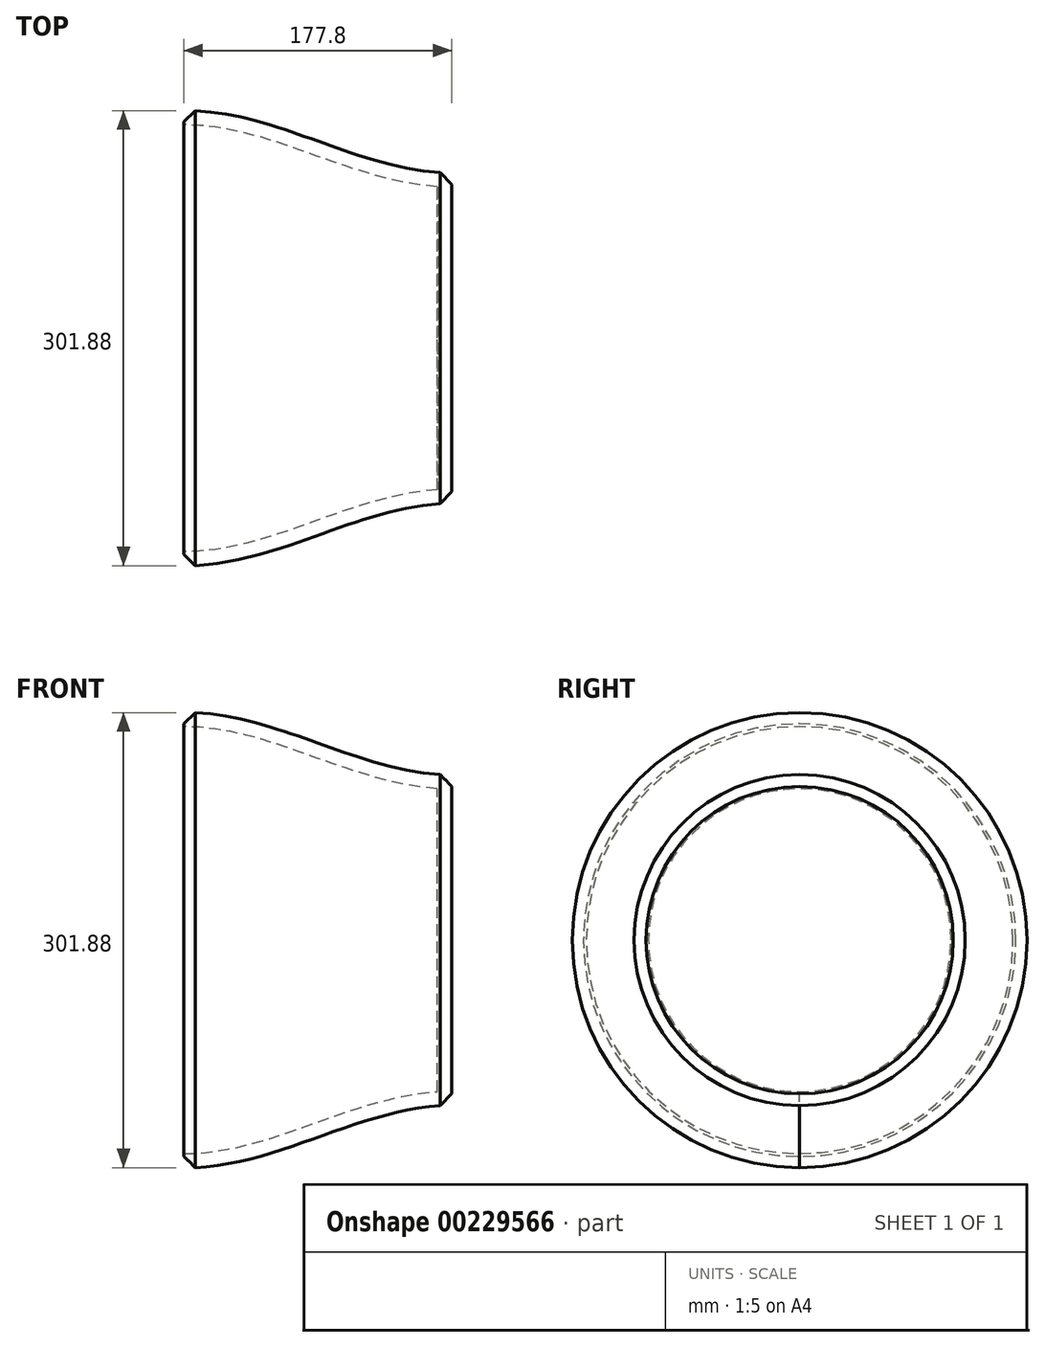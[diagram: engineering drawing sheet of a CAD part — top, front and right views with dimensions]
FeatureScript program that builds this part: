
annotation { "Feature Type Name" : "Feature", "Feature Type Description" : "" }
export const myFeature = defineFeature(function(context is Context, id is Id, definition is map)
    precondition{}
    {
        {
            var Q0;
            Q0=qCreatedBy(makeId("Front.planeOp"),FACE);
            var sketch = newSketch(context, id + "F0", { "sketchPlane" : qUnion([Q0])});
            skLineSegment(sketch, "E0", {"start": v(0, 0) * mm, "end": v(0, 151.13) * mm});
            skLineSegment(sketch, "E1", {"start": v(177.8, 109.54) * mm, "end": v(177.8, 0) * mm});
            skLineSegment(sketch, "E2", {"start": v(177.8, 0) * mm, "end": v(177.8, 109.54) * mm});
            skFitSpline(sketch, "E3", {"points": [v(0, 151.13) * mm, v(177.8, 109.54) * mm], "startDerivative": vector(189.64, 0) * mm, "endDerivative": vector(187.44, -2.85) * mm});
            skLineSegment(sketch, "E4", {"start": v(177.8, 0) * mm, "end": v(0, 0) * mm});
            skSolve(sketch);
        }
        {
            var Q0;
            Q0 = qSketchRegion(id + "F0", true);
            var Q1;
            Q1=sQuery(id+"F0.wireOp",EDGE,"E4");
            revolve(context, id + "F1", {"entities" : qUnion([Q0]), "axis" : qUnion([Q1]), "revolveType" : RevolveType.FULL});
        }
        {
            var Q0;
            Q0=makeQuery(id+"F1.opRevolve","SWEPT_FACE",FACE,{"disambiguationData":[OSD([sQuery(id+"F0.wireOp",EDGE,"E0")])]});
            var Q1;
            Q1=makeQuery(id+"F1.opRevolve","SWEPT_FACE",FACE,{"disambiguationData":[OSD([sQuery(id+"F0.wireOp",EDGE,"E2")])]});
            shell(context, id + "F2", {"entities" : qUnion([Q0, Q1]), "thickness" : 9.52 * mm});
        }
        {
            var Q0;
            Q0=makeQuery(id+"F1.opRevolve","SWEPT_EDGE",EDGE,{"disambiguationData":[OSD([sQuery(id+"F0.wireOp",EDGE,"E0"),sQuery(id+"F0.wireOp",EDGE,"E3")])]});
            var Q1;
            Q1=makeQuery(id+"F1.opRevolve","SWEPT_EDGE",EDGE,{"disambiguationData":[OSD([sQuery(id+"F0.wireOp",EDGE,"E2"),sQuery(id+"F0.wireOp",EDGE,"E3")])]});
            chamfer(context, id + "F3", {"entities" : qUnion([Q0, Q1]), "width" : 7.62 * mm, "tangentPropagation" : true});
        }
    });
